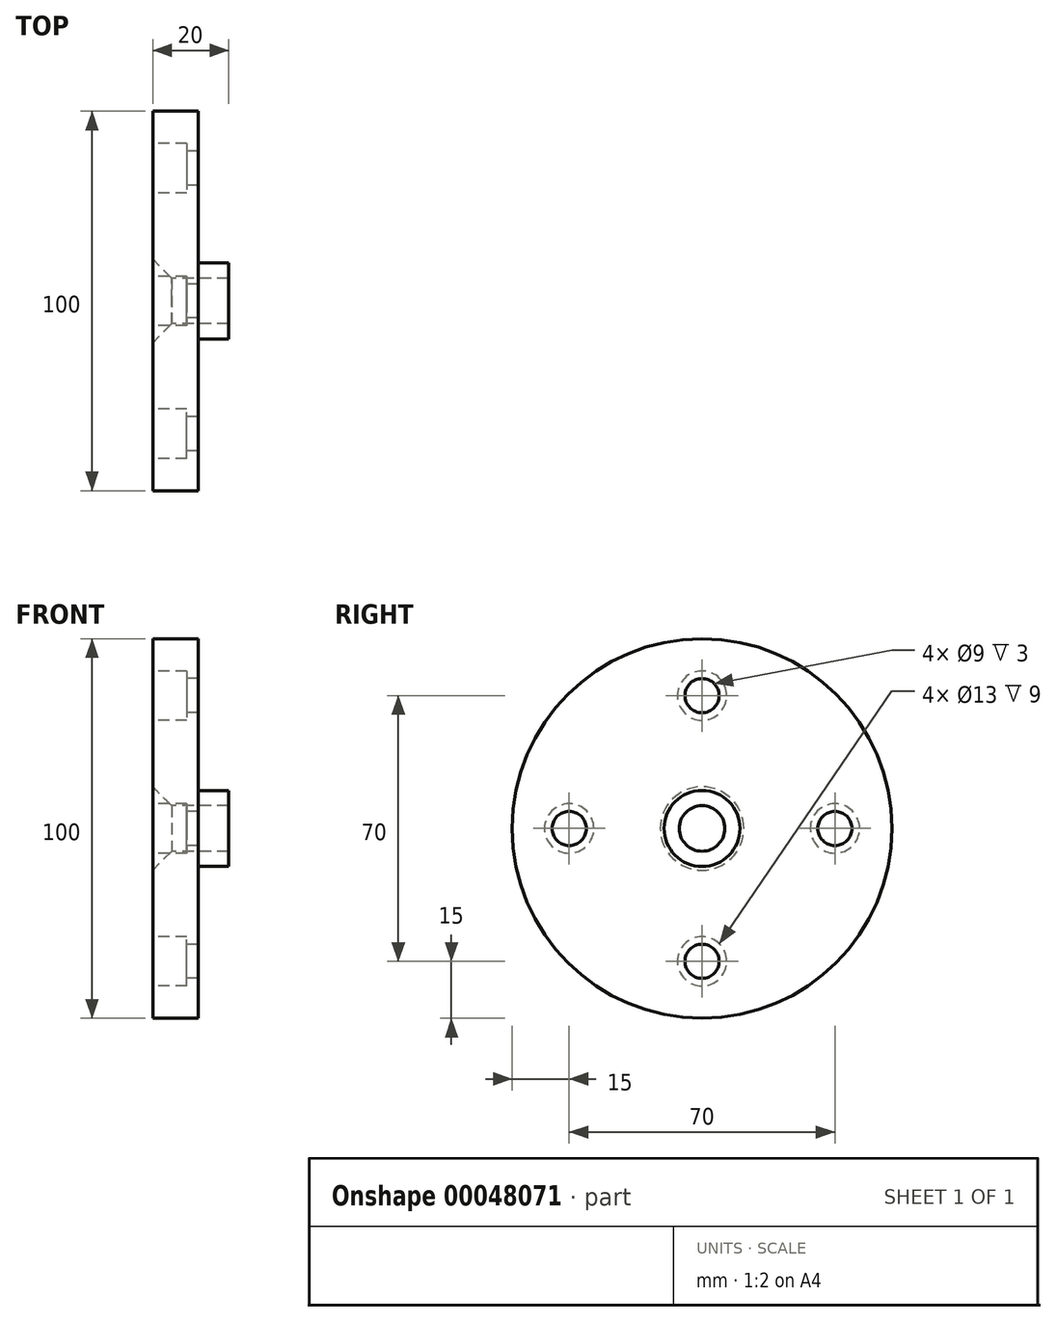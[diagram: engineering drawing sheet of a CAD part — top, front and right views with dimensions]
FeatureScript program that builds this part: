
annotation { "Feature Type Name" : "Feature", "Feature Type Description" : "" }
export const myFeature = defineFeature(function(context is Context, id is Id, definition is map)
    precondition{}
    {
        {
            var Q0;
            Q0=qCreatedBy(makeId("Front.planeOp"),FACE);
            var sketch = newSketch(context, id + "F0", { "sketchPlane" : qUnion([Q0])});
            skLineSegment(sketch, "E0", {"start": v(0, 0) * mm, "end": v(96.35, 0) * mm, "construction": true});
            skLineSegment(sketch, "E1", {"start": v(0, 6) * mm, "end": v(0, 50) * mm});
            skLineSegment(sketch, "E2", {"start": v(0, 50) * mm, "end": v(12, 50) * mm});
            skLineSegment(sketch, "E3", {"start": v(12, 50) * mm, "end": v(12, 10) * mm});
            skLineSegment(sketch, "E4", {"start": v(12, 10) * mm, "end": v(20, 10) * mm});
            skLineSegment(sketch, "E5", {"start": v(20, 10) * mm, "end": v(20, 6) * mm});
            skLineSegment(sketch, "E6", {"start": v(20, 6) * mm, "end": v(0, 6) * mm});
            skSolve(sketch);
        }
        {
            var Q0;
            Q0=makeQuery(id+"F0.imprint","IMPRINT",FACE,{"disambiguationData":[TD([[makeQuery(id+"F0.imprint","IMPRINT",EDGE,{"derivedFrom":sQuery(id+"F0.wireOp",EDGE,"E1")}),-1.0]])]});
            var Q1;
            Q1=sQuery(id+"F0.wireOp",EDGE,"E0");
            revolve(context, id + "F1", {"entities" : qUnion([Q0]), "axis" : qUnion([Q1]), "revolveType" : RevolveType.FULL});
        }
        {
            var Q0;
            Q0=makeQuery(id+"F1.opRevolve","SWEPT_FACE",FACE,{"disambiguationData":[OSD([sQuery(id+"F0.wireOp",EDGE,"E1")])]});
            var sketch = newSketch(context, id + "F2", { "sketchPlane" : qUnion([Q0])});
            skCircle(sketch, "E7", {"center": v(0, 0) * mm, "radius": 35 * mm, "construction": true});
            skCircle(sketch, "E8", {"center": v(0, 35) * mm, "radius": 4.5 * mm});
            skCircle(sketch, "E9", {"center": v(0, 35) * mm, "radius": 6.5 * mm});
            skSolve(sketch);
        }
        {
            var Q0;
            Q0 = qSketchRegion(id + "F2", true);
            extrude(context, id + "F3", {"entities" : qUnion([Q0]), "operationType" : NewBodyOperationType.REMOVE, "oppositeDirection" : true, "depth" : 9 * mm});
        }
        {
            var Q0;
            Q0=makeQuery(id+"F2.imprint","IMPRINT",FACE,{"disambiguationData":[TD([[makeQuery(id+"F2.imprint","IMPRINT",EDGE,{"derivedFrom":sQuery(id+"F2.wireOp",EDGE,"E8")}),1.0]])]});
            extrude(context, id + "F4", {"entities" : qUnion([Q0]), "operationType" : NewBodyOperationType.REMOVE, "oppositeDirection" : true, "depth" : 12 * mm});
        }
        {
            var Q0;
            Q0=makeQuery(id+"F3.boolean.opBoolean","COPY",FACE,{"derivedFrom":makeQuery(id+"F3.opExtrude","SWEPT_FACE",FACE,{"disambiguationData":[OSD([sQuery(id+"F2.wireOp",EDGE,"E9")])]})});
            var Q1;
            Q1=makeQuery(id+"F3.boolean.opBoolean","COPY",FACE,{"derivedFrom":makeQuery(id+"F3.opExtrude","CAP_FACE",FACE,{"disambiguationData":[OSD([sQuery(id+"F2.wireOp",EDGE,"E8"),sQuery(id+"F2.wireOp",EDGE,"E9")])],"isStart":false})});
            var Q2;
            Q2=makeQuery(id+"F4.boolean.opBoolean","COPY",FACE,{"derivedFrom":makeQuery(id+"F4.opExtrude","SWEPT_FACE",FACE,{"disambiguationData":[OSD([sQuery(id+"F2.wireOp",EDGE,"E8")])]})});
            var Q3;
            Q3=sQuery(id+"F0.wireOp",EDGE,"E0");
            circularPattern(context, id + "F5", {"faces" : qUnion([Q0, Q1, Q2]), "axis" : qUnion([Q3]), "angle" : 90 * degree, "instanceCount" : 4, "patternType" : PatternType.FACE});
        }
        {
            var Q0;
            Q0=makeQuery(id+"F1.opRevolve","SWEPT_EDGE",EDGE,{"disambiguationData":[OSD([sQuery(id+"F0.wireOp",EDGE,"E1"),sQuery(id+"F0.wireOp",EDGE,"E6")])]});
            chamfer(context, id + "F6", {"entities" : qUnion([Q0]), "width" : 5 * mm, "tangentPropagation" : true});
        }
    });
